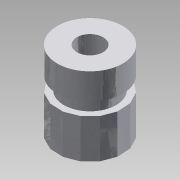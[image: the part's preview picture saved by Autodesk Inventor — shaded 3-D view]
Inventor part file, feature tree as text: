
AUTODESK INVENTOR PART (.ipt)
format: ipt  version: 2016 (Build 200138000, 138)  size: 138,240 bytes
history: native  units: mm
features: extrude x3, sketch x3, projected_geometry x2
ambient origin geometry x8: Origin, YZ Plane, XZ Plane, XY Plane, X Axis, Y Axis, Z Axis, Center Point
bodies: Solid1 (feature_tree)
feature tree (8):
  extrude  "Extrusion1"  Depth=3.0mm TaperAngle=0.0deg
  extrude  "Extrusion2"  Depth=1.0mm TaperAngle=0.0deg
  extrude  "Extrusion3"  Depth=2.0mm TaperAngle=0.0deg
  sketch  "Sketch1"  dims[d1=2.0mm d2=3.0mm d3=0.0mm]
  sketch  "Sketch2"  dims[d4=4.0mm d5=1.0mm d6=0.0mm]
  projected_geometry  "Projected Loop1"
  sketch  "Sketch3"  dims[d7=5.0mm d8=2.0mm d9=0.0mm]
  projected_geometry  "Projected Loop2"
